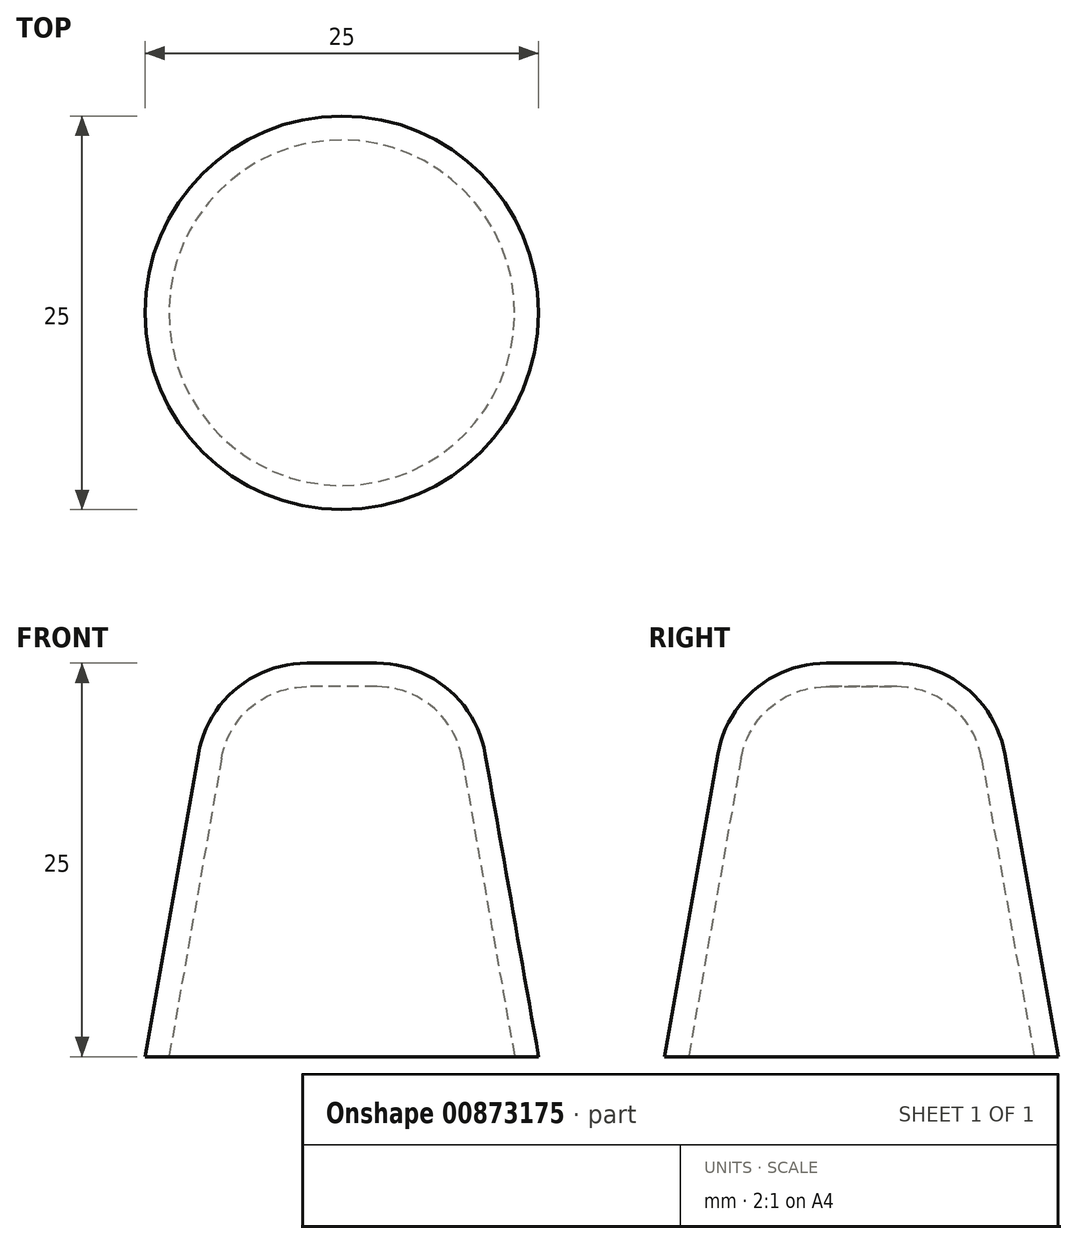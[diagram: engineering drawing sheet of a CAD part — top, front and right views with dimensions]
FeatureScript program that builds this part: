
annotation { "Feature Type Name" : "Feature", "Feature Type Description" : "" }
export const myFeature = defineFeature(function(context is Context, id is Id, definition is map)
    precondition{}
    {
        {
            var Q0;
            Q0=qCreatedBy(makeId("Top.planeOp"),FACE);
            var sketch = newSketch(context, id + "F0", { "sketchPlane" : qUnion([Q0])});
            skCircle(sketch, "E0", {"center": v(0, 0) * mm, "radius": 12.5 * mm});
            skSolve(sketch);
        }
        {
            var Q0;
            Q0 = qSketchRegion(id + "F0", true);
            extrude(context, id + "F1", {"entities" : qUnion([Q0]), "depth" : 25 * mm, "offsetDistance" : 25 * mm, "hasDraft" : true, "draftAngle" : 10 * degree, "draftPullDirection" : true});
        }
        {
            var Q0;
            Q0=makeQuery(id+"F1.opExtrude","CAP_FACE",FACE,{"disambiguationData":[OSD([sQuery(id+"F0.wireOp",EDGE,"E0")])],"isStart":false});
            fillet(context, id + "F2", {"entities" : qUnion([Q0]), "radius" : 7 * mm, "tangentPropagation" : true, "allowEdgeOverflow" : false});
        }
        {
            var Q0;
            Q0=makeQuery(id+"F1.opExtrude","CAP_FACE",FACE,{"disambiguationData":[OSD([sQuery(id+"F0.wireOp",EDGE,"E0")])],"isStart":true});
            shell(context, id + "F3", {"entities" : qUnion([Q0]), "thickness" : 1.5 * mm});
        }
    });
